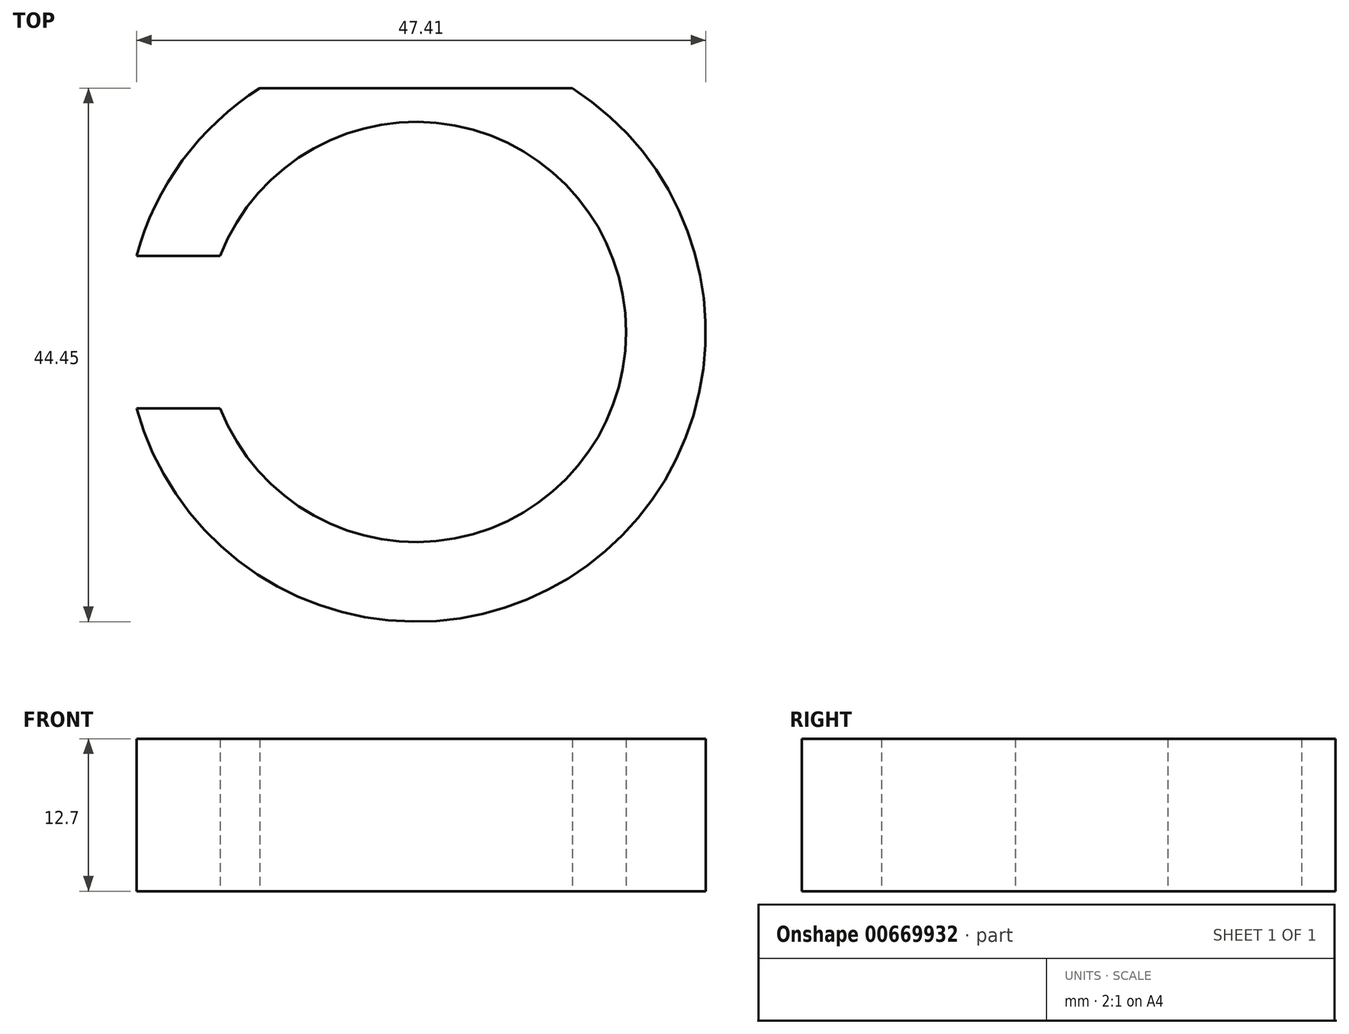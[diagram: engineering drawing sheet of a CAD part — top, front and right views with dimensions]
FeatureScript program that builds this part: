
annotation { "Feature Type Name" : "Feature", "Feature Type Description" : "" }
export const myFeature = defineFeature(function(context is Context, id is Id, definition is map)
    precondition{}
    {
        {
            var Q0;
            Q0=qCreatedBy(makeId("Top.planeOp"),FACE);
            var sketch = newSketch(context, id + "F0", { "sketchPlane" : qUnion([Q0])});
            skArc(sketch, "E0", {"start": v(-16.3, -6.35) * mm, "mid": v(17.5, 0) * mm, "end": v(-16.3, 6.35) * mm});
            skArc(sketch, "E1", {"start": v(-13.01, 20.32) * mm, "mid": v(-19.44, 14.29) * mm, "end": v(-23.28, 6.35) * mm});
            skLineSegment(sketch, "E2", {"start": v(-13.01, 20.32) * mm, "end": v(13.01, 20.32) * mm});
            skLineSegment(sketch, "E3", {"start": v(-23.28, -6.35) * mm, "end": v(-16.3, -6.35) * mm});
            skLineSegment(sketch, "E4", {"start": v(-23.28, 6.35) * mm, "end": v(-16.3, 6.35) * mm});
            skArc(sketch, "E5.trimOffspring", {"start": v(-23.28, -6.35) * mm, "mid": v(14.29, -19.44) * mm, "end": v(13.01, 20.32) * mm});
            skSolve(sketch);
        }
        {
            var Q0;
            Q0 = qSketchRegion(id + "F0", true);
            extrude(context, id + "F1", {"entities" : qUnion([Q0]), "depth" : 12.7 * mm, "offsetDistance" : 25.4 * mm});
        }
    });
